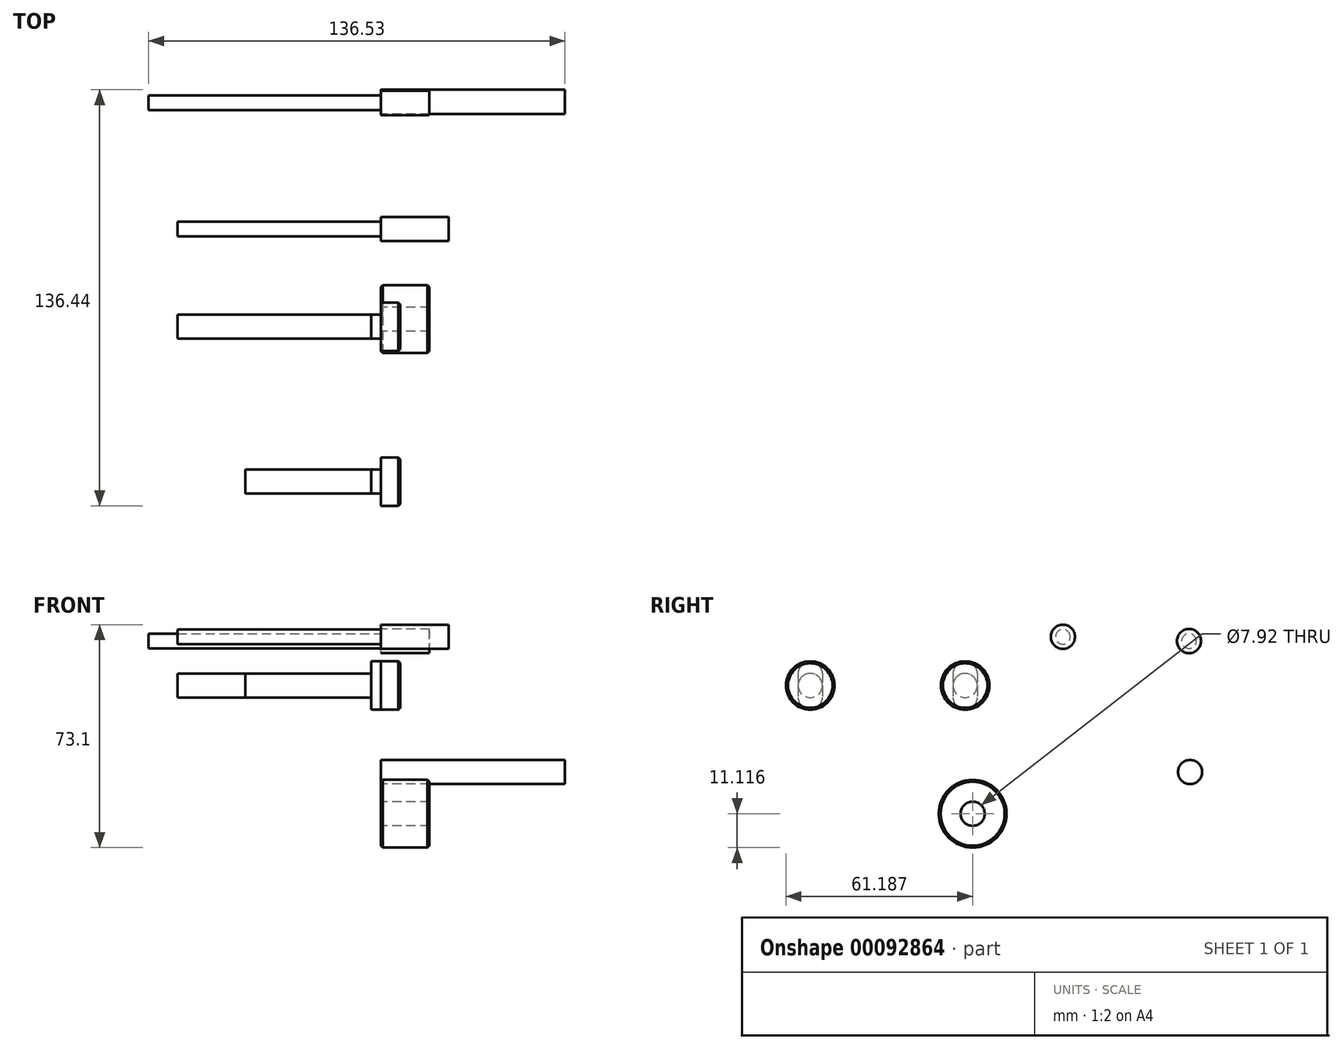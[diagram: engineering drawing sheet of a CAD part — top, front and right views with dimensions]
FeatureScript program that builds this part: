
annotation { "Feature Type Name" : "Feature", "Feature Type Description" : "" }
export const myFeature = defineFeature(function(context is Context, id is Id, definition is map)
    precondition{}
    {
        {
            var Q0;
            Q0=qCreatedBy(makeId("Right.planeOp"),FACE);
            var sketch = newSketch(context, id + "F0", { "sketchPlane" : qUnion([Q0])});
            skCircle(sketch, "E0", {"center": v(30.54, 35.15) * mm, "radius": 3.96 * mm});
            skSolve(sketch);
        }
        {
            var Q0;
            Q0=makeQuery(id+"F0.imprint","IMPRINT",FACE,{"disambiguationData":[TD([[makeQuery(id+"F0.imprint","IMPRINT",EDGE,{"derivedFrom":sQuery(id+"F0.wireOp",EDGE,"E0")}),1.0]])]});
            extrude(context, id + "F1", {"entities" : qUnion([Q0]), "depth" : 15.88 * mm});
        }
        {
            var Q0;
            Q0=qCreatedBy(makeId("Right.planeOp"),FACE);
            var sketch = newSketch(context, id + "F2", { "sketchPlane" : qUnion([Q0])});
            skCircle(sketch, "E1.0.0", {"center": v(30.54, 35.15) * mm, "radius": 3.96 * mm, "construction": true});
            skCircle(sketch, "E2", {"center": v(30.54, 35.15) * mm, "radius": 2.41 * mm});
            skSolve(sketch);
        }
        {
            var Q0;
            Q0=makeQuery(id+"F2.imprint","IMPRINT",FACE,{"disambiguationData":[TD([[makeQuery(id+"F2.imprint","IMPRINT",EDGE,{"derivedFrom":sQuery(id+"F2.wireOp",EDGE,"E2")}),1.0]])]});
            extrude(context, id + "F3", {"entities" : qUnion([Q0]), "operationType" : NewBodyOperationType.ADD, "oppositeDirection" : true, "depth" : 76.2 * mm});
        }
        {
            var Q0;
            Q0=qCreatedBy(makeId("Right.planeOp"),FACE);
            var sketch = newSketch(context, id + "F4", { "sketchPlane" : qUnion([Q0])});
            skCircle(sketch, "E3", {"center": v(-40.4, -21.47) * mm, "radius": 11.11 * mm});
            skCircle(sketch, "E4", {"center": v(-40.4, -21.47) * mm, "radius": 3.96 * mm});
            skSolve(sketch);
        }
        {
            var Q0;
            Q0=makeQuery(id+"F4.imprint","IMPRINT",FACE,{"disambiguationData":[TD([[makeQuery(id+"F4.imprint","IMPRINT",EDGE,{"derivedFrom":sQuery(id+"F4.wireOp",EDGE,"E3")}),1.0]])]});
            extrude(context, id + "F5", {"entities" : qUnion([Q0]), "depth" : 15.88 * mm});
        }
        {
            var Q0;
            Q0=makeQuery(id+"F5.opExtrude","CAP_EDGE",EDGE,{"disambiguationData":[OSD([sQuery(id+"F4.wireOp",EDGE,"E3")])],"isStart":false});
            var Q1;
            Q1=makeQuery(id+"F5.opExtrude","CAP_EDGE",EDGE,{"disambiguationData":[OSD([sQuery(id+"F4.wireOp",EDGE,"E3")])],"isStart":true});
            chamfer(context, id + "F6", {"entities" : qUnion([Q0, Q1]), "width" : 0.64 * mm, "tangentPropagation" : true});
        }
        {
            var Q0;
            Q0=qCreatedBy(makeId("Right.planeOp"),FACE);
            var sketch = newSketch(context, id + "F7", { "sketchPlane" : qUnion([Q0])});
            skCircle(sketch, "E5", {"center": v(-10.8, 36.55) * mm, "radius": 3.96 * mm});
            skSolve(sketch);
        }
        {
            var Q0;
            Q0=makeQuery(id+"F7.imprint","IMPRINT",FACE,{"disambiguationData":[TD([[makeQuery(id+"F7.imprint","IMPRINT",EDGE,{"derivedFrom":sQuery(id+"F7.wireOp",EDGE,"E5")}),1.0]])]});
            extrude(context, id + "F8", {"entities" : qUnion([Q0]), "depth" : 22.22 * mm});
        }
        {
            var Q0;
            Q0=makeQuery(id+"F8.opExtrude","CAP_FACE",FACE,{"disambiguationData":[OSD([sQuery(id+"F7.wireOp",EDGE,"E5")])],"isStart":true});
            var sketch = newSketch(context, id + "F9", { "sketchPlane" : qUnion([Q0])});
            skCircle(sketch, "E6.0.0", {"center": v(10.8, 36.55) * mm, "radius": 3.96 * mm, "construction": true});
            skCircle(sketch, "E7", {"center": v(10.8, 36.55) * mm, "radius": 2.41 * mm});
            skSolve(sketch);
        }
        {
            var Q0;
            Q0=makeQuery(id+"F9.imprint","IMPRINT",FACE,{"disambiguationData":[TD([[makeQuery(id+"F9.imprint","IMPRINT",EDGE,{"derivedFrom":sQuery(id+"F9.wireOp",EDGE,"E7")}),1.0]])]});
            extrude(context, id + "F10", {"entities" : qUnion([Q0]), "operationType" : NewBodyOperationType.ADD, "depth" : 66.67 * mm});
        }
        {
            var Q0;
            Q0=qCreatedBy(makeId("Right.planeOp"),FACE);
            var sketch = newSketch(context, id + "F11", { "sketchPlane" : qUnion([Q0])});
            skCircle(sketch, "E8", {"center": v(-42.85, 20.58) * mm, "radius": 7.94 * mm});
            skSolve(sketch);
        }
        {
            var Q0;
            Q0=makeQuery(id+"F11.imprint","IMPRINT",FACE,{"disambiguationData":[TD([[makeQuery(id+"F11.imprint","IMPRINT",EDGE,{"derivedFrom":sQuery(id+"F11.wireOp",EDGE,"E8")}),1.0]])]});
            extrude(context, id + "F12", {"entities" : qUnion([Q0]), "depth" : 6.35 * mm});
        }
        {
            var Q0;
            Q0=makeQuery(id+"F12.opExtrude","CAP_FACE",FACE,{"disambiguationData":[OSD([sQuery(id+"F11.wireOp",EDGE,"E8")])],"isStart":true});
            var sketch = newSketch(context, id + "F13", { "sketchPlane" : qUnion([Q0])});
            skCircle(sketch, "E9.0.0", {"center": v(42.85, 20.58) * mm, "radius": 7.94 * mm});
            skLineSegment(sketch, "E10", {"start": v(42.85, 24.55) * mm, "end": v(42.85, 16.6) * mm});
            skLineSegment(sketch, "E11", {"start": v(35.98, 24.55) * mm, "end": v(49.72, 24.55) * mm, "construction": true});
            skLineSegment(sketch, "E12", {"start": v(49.72, 16.6) * mm, "end": v(35.98, 16.6) * mm, "construction": true});
            skPoint(sketch, "E13.orphan", {"position": v(42.85, 28.52) * mm});
            skPoint(sketch, "E14.orphan", {"position": v(42.85, 12.64) * mm});
            skArc(sketch, "E15.0.startCap", {"start": v(38.89, 24.55) * mm, "mid": v(42.85, 28.52) * mm, "end": v(46.81, 24.55) * mm});
            skArc(sketch, "E15.0.endCap", {"start": v(46.81, 16.6) * mm, "mid": v(42.85, 12.64) * mm, "end": v(38.89, 16.6) * mm});
            skLineSegment(sketch, "E15.0.left", {"start": v(46.81, 24.55) * mm, "end": v(46.81, 16.6) * mm});
            skLineSegment(sketch, "E15.0.right", {"start": v(38.89, 24.55) * mm, "end": v(38.89, 16.6) * mm});
            skSolve(sketch);
        }
        {
            var Q0;
            {var subQ4=sQuery(id+"F13.wireOp",EDGE,"E15.0.left");Q0=makeQuery(id+"F13.imprint","IMPRINT",FACE,{"disambiguationData":[TD([[makeQuery(id+"F13.imprint","IMPRINT",EDGE,{"derivedFrom":subQ4}),-1.0]])]});}
            extrude(context, id + "F14", {"entities" : qUnion([Q0]), "operationType" : NewBodyOperationType.ADD, "depth" : 3.17 * mm});
        }
        {
            var Q0;
            Q0=makeQuery(id+"F14.opExtrude","CAP_FACE",FACE,{"disambiguationData":[OSD([sQuery(id+"F13.wireOp",EDGE,"E15.0.startCap"),sQuery(id+"F13.wireOp",EDGE,"E15.0.endCap"),sQuery(id+"F13.wireOp",EDGE,"E15.0.left"),sQuery(id+"F13.wireOp",EDGE,"E15.0.right")])],"isStart":false});
            var sketch = newSketch(context, id + "F15", { "sketchPlane" : qUnion([Q0])});
            skLineSegment(sketch, "E16.0.0", {"start": v(38.89, 16.6) * mm, "end": v(38.89, 24.55) * mm});
            skArc(sketch, "E16.0.1", {"start": v(38.89, 24.55) * mm, "mid": v(40.05, 27.35) * mm, "end": v(42.85, 28.52) * mm});
            skArc(sketch, "E16.0.2", {"start": v(42.85, 28.52) * mm, "mid": v(34.91, 20.58) * mm, "end": v(42.85, 12.64) * mm});
            skArc(sketch, "E16.0.3", {"start": v(42.85, 12.64) * mm, "mid": v(40.05, 13.8) * mm, "end": v(38.89, 16.6) * mm});
            skCircle(sketch, "E17", {"center": v(42.85, 20.58) * mm, "radius": 3.96 * mm});
            skSolve(sketch);
        }
        {
            var Q0;
            {var subQ0=sQuery(id+"F15.wireOp",EDGE,"E17");var subQ1=makeQuery(id+"F15.imprint","INTERSECT",VERTEX,{"derivedFrom":[sQuery(id+"F15.wireOp",EDGE,"E16.0.0"),subQ0]});Q0=makeQuery(id+"F15.imprint","IMPRINT",FACE,{"disambiguationData":[TD([[makeQuery(id+"F15.imprint","IMPRINT",EDGE,{"disambiguationData":[TD([[subQ1,1.0]])],"derivedFrom":subQ0}),1.0]])]});}
            extrude(context, id + "F16", {"entities" : qUnion([Q0]), "operationType" : NewBodyOperationType.ADD, "depth" : 63.5 * mm});
        }
        {
            var Q0;
            Q0=makeQuery(id+"F12.opExtrude","SWEPT_BODY",BODY,{"disambiguationData":[OSD([sQuery(id+"F11.wireOp",EDGE,"E8")])]});
            var Q1;
            Q1=qCreatedBy(makeId("Front.planeOp"),FACE);
            transform(context, id + "F17", {"entities" : qUnion([Q0]), "transformType" : TransformType.TRANSLATION_DISTANCE, "transformDirection" : qUnion([Q1]), "distance" : 50.8 * mm, "makeCopy" : true});
        }
        {
            var Q0;
            Q0=makeQuery(id+"F17.opPattern","COPY",FACE,{"derivedFrom":makeQuery(id+"F16.opExtrude","CAP_FACE",FACE,{"disambiguationData":[OSD([sQuery(id+"F15.wireOp",EDGE,"E17")])],"isStart":false}),"instanceName":"1"});
            extrude(context, id + "F18", {"entities" : qUnion([Q0]), "operationType" : NewBodyOperationType.REMOVE, "oppositeDirection" : true, "depth" : 22.22 * mm});
        }
        {
            var Q0;
            Q0=qCreatedBy(makeId("Right.planeOp"),FACE);
            var sketch = newSketch(context, id + "F19", { "sketchPlane" : qUnion([Q0])});
            skCircle(sketch, "E18", {"center": v(30.9, -7.8) * mm, "radius": 3.96 * mm});
            skSolve(sketch);
        }
        {
            var Q0;
            Q0=makeQuery(id+"F19.imprint","IMPRINT",FACE,{"disambiguationData":[TD([[makeQuery(id+"F19.imprint","IMPRINT",EDGE,{"derivedFrom":sQuery(id+"F19.wireOp",EDGE,"E18")}),1.0]])]});
            extrude(context, id + "F20", {"entities" : qUnion([Q0]), "depth" : 60.32 * mm});
        }
        {
            var Q0;
            Q0=makeQuery(id+"F12.opExtrude","CAP_EDGE",EDGE,{"disambiguationData":[OSD([sQuery(id+"F11.wireOp",EDGE,"E8")])],"isStart":false});
            var Q1;
            Q1=makeQuery(id+"F17.opPattern","COPY",EDGE,{"derivedFrom":makeQuery(id+"F12.opExtrude","CAP_EDGE",EDGE,{"disambiguationData":[OSD([sQuery(id+"F11.wireOp",EDGE,"E8")])],"isStart":false}),"instanceName":"1"});
            chamfer(context, id + "F21", {"entities" : qUnion([Q0, Q1]), "width" : 0.64 * mm, "tangentPropagation" : true});
        }
    });
